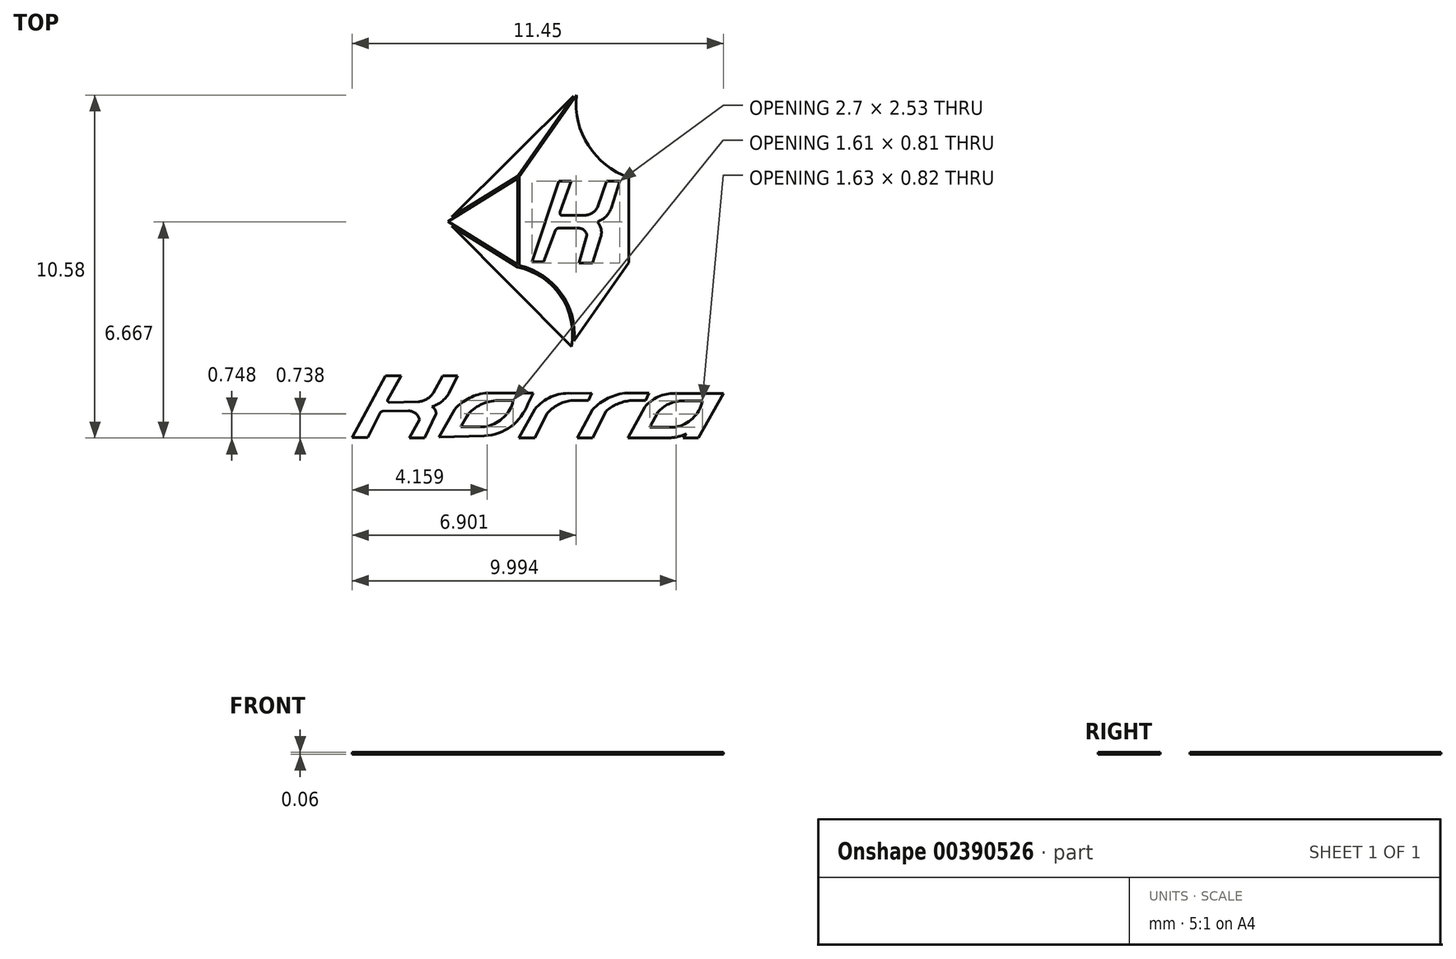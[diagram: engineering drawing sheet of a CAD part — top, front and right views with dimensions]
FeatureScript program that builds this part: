
annotation { "Feature Type Name" : "Feature", "Feature Type Description" : "" }
export const myFeature = defineFeature(function(context is Context, id is Id, definition is map)
    precondition{}
    {
        {
            var Q0;
            Q0=qCreatedBy(makeId("Top.planeOp"),FACE);
            var sketch = newSketch(context, id + "F0", { "sketchPlane" : qUnion([Q0])});
            skLineSegment(sketch, "E0", {"start": v(-5.5, 15.48) * mm, "end": v(-5.5, 6.6) * mm});
            skLineSegment(sketch, "E1", {"start": v(-5.5, 6.36) * mm, "end": v(-12.27, 10.6) * mm});
            skLineSegment(sketch, "E2", {"start": v(-5.5, 15.71) * mm, "end": v(-12.26, 11.53) * mm});
            skLineSegment(sketch, "E3", {"start": v(0.24, 23.94) * mm, "end": v(-5.5, 15.71) * mm});
            skLineSegment(sketch, "E4", {"start": v(0.88, 24.86) * mm, "end": v(-13.01, 11.06) * mm});
            skLineSegment(sketch, "E5", {"start": v(-13.01, 11.06) * mm, "end": v(0, -2.05) * mm});
            skLineSegment(sketch, "E6", {"start": v(0, -2.05) * mm, "end": v(6.14, 6.74) * mm});
            skLineSegment(sketch, "E7", {"start": v(6.14, 6.74) * mm, "end": v(6.14, 15.71) * mm});
            skArc(sketch, "E8", {"start": v(0.88, 24.86) * mm, "mid": v(1.76, 19.28) * mm, "end": v(6.14, 15.71) * mm});
            skArc(sketch, "E9", {"start": v(0.05, -1.81) * mm, "mid": v(-1.08, 3.4) * mm, "end": v(-5.5, 6.36) * mm});
            skLineSegment(sketch, "E10.0", {"start": v(5.94, 6.74) * mm, "end": v(5.94, 15.57) * mm});
            skArc(sketch, "E11.0", {"start": v(0.32, -1.24) * mm, "mid": v(-1.04, 3.7) * mm, "end": v(-5.3, 6.52) * mm});
            skLineSegment(sketch, "E12.0", {"start": v(-5.3, 15.65) * mm, "end": v(-5.3, 6.52) * mm});
            skLineSegment(sketch, "E13.0", {"start": v(0.55, 24.03) * mm, "end": v(-5.3, 15.65) * mm});
            skArc(sketch, "E14.trimOffspring", {"start": v(0.55, 24.03) * mm, "mid": v(1.77, 18.86) * mm, "end": v(5.94, 15.57) * mm});
            skLineSegment(sketch, "E15.trimOffspring", {"start": v(0.32, -1.24) * mm, "end": v(5.97, 6.85) * mm});
            skLineSegment(sketch, "E16.0", {"start": v(0.24, 23.94) * mm, "end": v(-12.26, 11.53) * mm});
            skLineSegment(sketch, "E17.0", {"start": v(-5.5, 15.48) * mm, "end": v(-12.64, 11.06) * mm});
            skLineSegment(sketch, "E18.0", {"start": v(-5.5, 6.6) * mm, "end": v(-12.64, 11.06) * mm});
            skLineSegment(sketch, "E19.trimOffspring", {"start": v(-12.27, 10.6) * mm, "end": v(0.05, -1.81) * mm});
            skLineSegment(sketch, "E20", {"start": v(-1.26, 15.2) * mm, "end": v(-4, 6.89) * mm});
            skLineSegment(sketch, "E21", {"start": v(-4, 6.89) * mm, "end": v(-2.81, 6.89) * mm});
            skLineSegment(sketch, "E22", {"start": v(-1.26, 15.2) * mm, "end": v(0, 15.2) * mm});
            skLineSegment(sketch, "E23", {"start": v(0, 15.2) * mm, "end": v(-1.26, 11.68) * mm});
            skLineSegment(sketch, "E24", {"start": v(-1.26, 11.68) * mm, "end": v(1.4, 11.68) * mm});
            skLineSegment(sketch, "E25", {"start": v(3.63, 15.18) * mm, "end": v(2.75, 12.6) * mm});
            skLineSegment(sketch, "E26", {"start": v(3.63, 15.18) * mm, "end": v(5.01, 15.18) * mm});
            skLineSegment(sketch, "E27", {"start": v(5.01, 15.18) * mm, "end": v(4.14, 12.47) * mm});
            skLineSegment(sketch, "E28", {"start": v(-2.81, 6.89) * mm, "end": v(-1.52, 10.35) * mm});
            skLineSegment(sketch, "E29", {"start": v(-1.52, 10.35) * mm, "end": v(0.78, 10.35) * mm});
            skLineSegment(sketch, "E30", {"start": v(1.64, 9.59) * mm, "end": v(0.82, 6.78) * mm});
            skLineSegment(sketch, "E31", {"start": v(0.82, 6.78) * mm, "end": v(2.2, 6.78) * mm});
            skLineSegment(sketch, "E32", {"start": v(2.2, 6.78) * mm, "end": v(3.05, 9.47) * mm});
            skArc(sketch, "E33", {"start": v(1.4, 11.68) * mm, "mid": v(2.22, 11.93) * mm, "end": v(2.75, 12.6) * mm});
            skArc(sketch, "E34", {"start": v(2.7, 11) * mm, "mid": v(3.6, 11.57) * mm, "end": v(4.14, 12.47) * mm});
            skArc(sketch, "E35", {"start": v(3.05, 9.47) * mm, "mid": v(3.09, 10.28) * mm, "end": v(2.7, 11) * mm});
            skArc(sketch, "E36", {"start": v(1.64, 9.59) * mm, "mid": v(1.36, 10.13) * mm, "end": v(0.78, 10.35) * mm});
            skArc(sketch, "E37", {"start": v(-1.13, 12.04) * mm, "mid": v(-1.13, 11.84) * mm, "end": v(-1.03, 11.68) * mm});
            skArc(sketch, "E38", {"start": v(-1.3, 10.35) * mm, "mid": v(-1.48, 10.29) * mm, "end": v(-1.6, 10.15) * mm});
            skArc(sketch, "E39", {"start": v(-15.71, -7.5) * mm, "mid": v(-14.84, -7.23) * mm, "end": v(-14.17, -6.61) * mm});
            skArc(sketch, "E40", {"start": v(-14.3, -8) * mm, "mid": v(-13.31, -7.49) * mm, "end": v(-12.58, -6.65) * mm});
            skArc(sketch, "E41", {"start": v(-13.9, -8.8) * mm, "mid": v(-13.97, -8.34) * mm, "end": v(-14.3, -8) * mm});
            skArc(sketch, "E42", {"start": v(-18.88, -7.32) * mm, "mid": v(-18.84, -7.48) * mm, "end": v(-18.7, -7.56) * mm});
            skArc(sketch, "E43", {"start": v(-19.32, -8.46) * mm, "mid": v(-19.54, -8.55) * mm, "end": v(-19.69, -8.73) * mm});
            skArc(sketch, "E44", {"start": v(-8.6, -6.6) * mm, "mid": v(-10.45, -7.12) * mm, "end": v(-11.96, -8.29) * mm});
            skArc(sketch, "E45", {"start": v(-8.87, -10.1) * mm, "mid": v(-7.09, -9.25) * mm, "end": v(-5.99, -7.62) * mm});
            skArc(sketch, "E46", {"start": v(0, -7.39) * mm, "mid": v(-1.37, -7.83) * mm, "end": v(-2.49, -8.74) * mm});
            skArc(sketch, "E47", {"start": v(0, -6.63) * mm, "mid": v(-2.05, -7.01) * mm, "end": v(-3.71, -8.27) * mm});
            skArc(sketch, "E48", {"start": v(5.75, -6.6) * mm, "mid": v(3.83, -7.13) * mm, "end": v(2.22, -8.31) * mm});
            skArc(sketch, "E49", {"start": v(6.05, -7.39) * mm, "mid": v(4.75, -7.75) * mm, "end": v(3.62, -8.46) * mm});
            skArc(sketch, "E50", {"start": v(10.64, -6.63) * mm, "mid": v(8.96, -7) * mm, "end": v(7.57, -8.03) * mm});
            skArc(sketch, "E51", {"start": v(11.38, -7.4) * mm, "mid": v(10.04, -7.74) * mm, "end": v(8.95, -8.57) * mm});
            skArc(sketch, "E52", {"start": v(10.45, -10.14) * mm, "mid": v(12.32, -9.38) * mm, "end": v(13.44, -7.7) * mm});
            skArc(sketch, "E53", {"start": v(-8.92, -11) * mm, "mid": v(-6.17, -10.04) * mm, "end": v(-4.44, -7.7) * mm});
            skLineSegment(sketch, "E54", {"start": v(-8.6, -6.6) * mm, "end": v(-3.9, -6.6) * mm});
            skLineSegment(sketch, "E55", {"start": v(-3.9, -6.6) * mm, "end": v(-4.44, -7.7) * mm});
            skLineSegment(sketch, "E56", {"start": v(-8.92, -11) * mm, "end": v(-13.57, -11.15) * mm});
            skLineSegment(sketch, "E57", {"start": v(-13.57, -11.15) * mm, "end": v(-11.96, -8.29) * mm});
            skLineSegment(sketch, "E58", {"start": v(-7.5, -7.39) * mm, "end": v(-5.95, -7.39) * mm});
            skLineSegment(sketch, "E59", {"start": v(-5.95, -7.39) * mm, "end": v(-5.99, -7.62) * mm});
            skLineSegment(sketch, "E60", {"start": v(-8.87, -10.1) * mm, "end": v(-11.33, -10.1) * mm});
            skLineSegment(sketch, "E61", {"start": v(-11.33, -10.1) * mm, "end": v(-10.72, -8.97) * mm});
            skArc(sketch, "E62", {"start": v(-7.5, -7.39) * mm, "mid": v(-9.29, -7.8) * mm, "end": v(-10.72, -8.97) * mm});
            skLineSegment(sketch, "E63", {"start": v(-19.07, -4.84) * mm, "end": v(-22.5, -11.18) * mm});
            skLineSegment(sketch, "E64", {"start": v(-22.5, -11.18) * mm, "end": v(-20.9, -11.18) * mm});
            skLineSegment(sketch, "E65", {"start": v(-20.9, -11.18) * mm, "end": v(-19.69, -8.73) * mm});
            skLineSegment(sketch, "E66", {"start": v(-19.32, -8.46) * mm, "end": v(-16.7, -8.44) * mm});
            skLineSegment(sketch, "E67", {"start": v(-16.62, -11.21) * mm, "end": v(-15.58, -9.33) * mm});
            skArc(sketch, "E68", {"start": v(-15.58, -9.33) * mm, "mid": v(-15.99, -8.69) * mm, "end": v(-16.7, -8.44) * mm});
            skLineSegment(sketch, "E69", {"start": v(-16.62, -11.21) * mm, "end": v(-15.07, -11.21) * mm});
            skLineSegment(sketch, "E70", {"start": v(-15.07, -11.21) * mm, "end": v(-13.9, -8.8) * mm});
            skLineSegment(sketch, "E71", {"start": v(-19.07, -4.84) * mm, "end": v(-17.47, -4.84) * mm});
            skLineSegment(sketch, "E72", {"start": v(-17.47, -4.84) * mm, "end": v(-18.88, -7.32) * mm});
            skLineSegment(sketch, "E73", {"start": v(-18.7, -7.56) * mm, "end": v(-15.71, -7.5) * mm});
            skLineSegment(sketch, "E74", {"start": v(-14.17, -6.61) * mm, "end": v(-13.21, -4.84) * mm});
            skLineSegment(sketch, "E75", {"start": v(-13.21, -4.84) * mm, "end": v(-11.68, -4.84) * mm});
            skLineSegment(sketch, "E76", {"start": v(-11.68, -4.84) * mm, "end": v(-12.58, -6.65) * mm});
            skLineSegment(sketch, "E77", {"start": v(-3.71, -8.27) * mm, "end": v(-5.37, -11.21) * mm});
            skLineSegment(sketch, "E78", {"start": v(-5.37, -11.21) * mm, "end": v(-3.71, -11.24) * mm});
            skLineSegment(sketch, "E79", {"start": v(-3.71, -11.24) * mm, "end": v(-2.49, -8.74) * mm});
            skLineSegment(sketch, "E80", {"start": v(0, -6.63) * mm, "end": v(2.12, -6.61) * mm});
            skLineSegment(sketch, "E81", {"start": v(2.12, -6.61) * mm, "end": v(1.79, -7.39) * mm});
            skLineSegment(sketch, "E82", {"start": v(1.79, -7.39) * mm, "end": v(0, -7.39) * mm});
            skLineSegment(sketch, "E83", {"start": v(2.22, -8.31) * mm, "end": v(0.66, -11.21) * mm});
            skLineSegment(sketch, "E84", {"start": v(0.66, -11.21) * mm, "end": v(2.22, -11.24) * mm});
            skLineSegment(sketch, "E85", {"start": v(2.22, -11.24) * mm, "end": v(3.62, -8.46) * mm});
            skLineSegment(sketch, "E86", {"start": v(5.75, -6.6) * mm, "end": v(8, -6.61) * mm});
            skLineSegment(sketch, "E87", {"start": v(8, -6.61) * mm, "end": v(7.66, -7.39) * mm});
            skLineSegment(sketch, "E88", {"start": v(7.66, -7.39) * mm, "end": v(6.05, -7.39) * mm});
            skLineSegment(sketch, "E89", {"start": v(7.57, -8.03) * mm, "end": v(5.84, -11.24) * mm});
            skLineSegment(sketch, "E90", {"start": v(5.84, -11.24) * mm, "end": v(10.03, -11.21) * mm});
            skLineSegment(sketch, "E91", {"start": v(10.64, -6.63) * mm, "end": v(15.67, -6.64) * mm});
            skLineSegment(sketch, "E92", {"start": v(15.67, -6.64) * mm, "end": v(13.07, -11.21) * mm});
            skLineSegment(sketch, "E93", {"start": v(13.07, -11.21) * mm, "end": v(11.54, -11.21) * mm});
            skLineSegment(sketch, "E94", {"start": v(11.54, -11.21) * mm, "end": v(11.86, -10.78) * mm});
            skArc(sketch, "E95", {"start": v(10.03, -11.21) * mm, "mid": v(10.97, -11.1) * mm, "end": v(11.86, -10.78) * mm});
            skLineSegment(sketch, "E96", {"start": v(11.38, -7.4) * mm, "end": v(13.52, -7.4) * mm});
            skLineSegment(sketch, "E97", {"start": v(13.52, -7.4) * mm, "end": v(13.44, -7.7) * mm});
            skLineSegment(sketch, "E98", {"start": v(10.45, -10.14) * mm, "end": v(8.1, -10.14) * mm});
            skLineSegment(sketch, "E99", {"start": v(8.1, -10.14) * mm, "end": v(8.95, -8.57) * mm});
            skSolve(sketch);
        }
        {
            var Q0;
            {var subQ8=sQuery(id+"F0.wireOp",EDGE,"E11.0");Q0=makeQuery(id+"F0.imprint","IMPRINT",FACE,{"disambiguationData":[TD([[makeQuery(id+"F0.imprint","IMPRINT",EDGE,{"derivedFrom":subQ8}),-1.0]])]});}
            var Q1;
            Q1=makeQuery(id+"F0.imprint","IMPRINT",FACE,{"disambiguationData":[TD([[makeQuery(id+"F0.imprint","IMPRINT",EDGE,{"derivedFrom":sQuery(id+"F0.wireOp",EDGE,"E1")}),1.0]])]});
            var Q2;
            Q2=makeQuery(id+"F0.imprint","IMPRINT",FACE,{"disambiguationData":[TD([[makeQuery(id+"F0.imprint","IMPRINT",EDGE,{"derivedFrom":sQuery(id+"F0.wireOp",EDGE,"E0")}),-1.0]])]});
            var Q3;
            Q3=makeQuery(id+"F0.imprint","IMPRINT",FACE,{"disambiguationData":[TD([[makeQuery(id+"F0.imprint","IMPRINT",EDGE,{"derivedFrom":sQuery(id+"F0.wireOp",EDGE,"E2")}),-1.0]])]});
            var Q4;
            Q4=makeQuery(id+"F0.imprint","IMPRINT",FACE,{"disambiguationData":[TD([[makeQuery(id+"F0.imprint","IMPRINT",EDGE,{"derivedFrom":sQuery(id+"F0.wireOp",EDGE,"E50")}),1.0]])]});
            var Q5;
            Q5=makeQuery(id+"F0.imprint","IMPRINT",FACE,{"disambiguationData":[TD([[makeQuery(id+"F0.imprint","IMPRINT",EDGE,{"derivedFrom":sQuery(id+"F0.wireOp",EDGE,"E48")}),1.0]])]});
            var Q6;
            Q6=makeQuery(id+"F0.imprint","IMPRINT",FACE,{"disambiguationData":[TD([[makeQuery(id+"F0.imprint","IMPRINT",EDGE,{"derivedFrom":sQuery(id+"F0.wireOp",EDGE,"E46")}),-1.0]])]});
            var Q7;
            Q7=makeQuery(id+"F0.imprint","IMPRINT",FACE,{"disambiguationData":[TD([[makeQuery(id+"F0.imprint","IMPRINT",EDGE,{"derivedFrom":sQuery(id+"F0.wireOp",EDGE,"E44")}),1.0]])]});
            var Q8;
            Q8=makeQuery(id+"F0.imprint","IMPRINT",FACE,{"disambiguationData":[TD([[makeQuery(id+"F0.imprint","IMPRINT",EDGE,{"derivedFrom":sQuery(id+"F0.wireOp",EDGE,"E39")}),-1.0]])]});
            extrude(context, id + "F1", {"entities" : qUnion([Q0, Q1, Q2, Q3, Q4, Q5, Q6, Q7, Q8]), "oppositeDirection" : true, "depth" : .2 * mm});
        }
        {
            var Q0;
            Q0=makeQuery(id+"F1.opExtrude","SWEPT_BODY",BODY,{"disambiguationData":[OSD([sQuery(id+"F0.wireOp",EDGE,"E1"),sQuery(id+"F0.wireOp",EDGE,"E9"),sQuery(id+"F0.wireOp",EDGE,"E19.trimOffspring")])]});
            var Q1;
            Q1=makeQuery(id+"F1.opExtrude","SWEPT_BODY",BODY,{"disambiguationData":[OSD([sQuery(id+"F0.wireOp",EDGE,"E39"),sQuery(id+"F0.wireOp",EDGE,"E40"),sQuery(id+"F0.wireOp",EDGE,"E41"),sQuery(id+"F0.wireOp",EDGE,"E42"),sQuery(id+"F0.wireOp",EDGE,"E43"),sQuery(id+"F0.wireOp",EDGE,"E63"),sQuery(id+"F0.wireOp",EDGE,"E64"),sQuery(id+"F0.wireOp",EDGE,"E65"),sQuery(id+"F0.wireOp",EDGE,"E66"),sQuery(id+"F0.wireOp",EDGE,"E67"),sQuery(id+"F0.wireOp",EDGE,"E68"),sQuery(id+"F0.wireOp",EDGE,"E69"),sQuery(id+"F0.wireOp",EDGE,"E70"),sQuery(id+"F0.wireOp",EDGE,"E71"),sQuery(id+"F0.wireOp",EDGE,"E72"),sQuery(id+"F0.wireOp",EDGE,"E73"),sQuery(id+"F0.wireOp",EDGE,"E74"),sQuery(id+"F0.wireOp",EDGE,"E75"),sQuery(id+"F0.wireOp",EDGE,"E76")])]});
            var Q2;
            Q2=makeQuery(id+"F1.opExtrude","SWEPT_BODY",BODY,{"disambiguationData":[OSD([sQuery(id+"F0.wireOp",EDGE,"E44"),sQuery(id+"F0.wireOp",EDGE,"E45"),sQuery(id+"F0.wireOp",EDGE,"E53"),sQuery(id+"F0.wireOp",EDGE,"E54"),sQuery(id+"F0.wireOp",EDGE,"E55"),sQuery(id+"F0.wireOp",EDGE,"E56"),sQuery(id+"F0.wireOp",EDGE,"E57"),sQuery(id+"F0.wireOp",EDGE,"E58"),sQuery(id+"F0.wireOp",EDGE,"E59"),sQuery(id+"F0.wireOp",EDGE,"E60"),sQuery(id+"F0.wireOp",EDGE,"E61"),sQuery(id+"F0.wireOp",EDGE,"E62")])]});
            var Q3;
            Q3=makeQuery(id+"F1.opExtrude","SWEPT_BODY",BODY,{"disambiguationData":[OSD([sQuery(id+"F0.wireOp",EDGE,"E46"),sQuery(id+"F0.wireOp",EDGE,"E47"),sQuery(id+"F0.wireOp",EDGE,"E77"),sQuery(id+"F0.wireOp",EDGE,"E78"),sQuery(id+"F0.wireOp",EDGE,"E79"),sQuery(id+"F0.wireOp",EDGE,"E80"),sQuery(id+"F0.wireOp",EDGE,"E81"),sQuery(id+"F0.wireOp",EDGE,"E82")])]});
            var Q4;
            Q4=makeQuery(id+"F1.opExtrude","SWEPT_BODY",BODY,{"disambiguationData":[OSD([sQuery(id+"F0.wireOp",EDGE,"E0"),sQuery(id+"F0.wireOp",EDGE,"E17.0"),sQuery(id+"F0.wireOp",EDGE,"E18.0")])]});
            var Q5;
            Q5=makeQuery(id+"F1.opExtrude","SWEPT_BODY",BODY,{"disambiguationData":[OSD([sQuery(id+"F0.wireOp",EDGE,"E2"),sQuery(id+"F0.wireOp",EDGE,"E3"),sQuery(id+"F0.wireOp",EDGE,"E16.0")])]});
            var Q6;
            Q6=makeQuery(id+"F1.opExtrude","SWEPT_BODY",BODY,{"disambiguationData":[OSD([sQuery(id+"F0.wireOp",EDGE,"E10.0"),sQuery(id+"F0.wireOp",EDGE,"E11.0"),sQuery(id+"F0.wireOp",EDGE,"E12.0"),sQuery(id+"F0.wireOp",EDGE,"E13.0"),sQuery(id+"F0.wireOp",EDGE,"E14.trimOffspring"),sQuery(id+"F0.wireOp",EDGE,"E15.trimOffspring"),sQuery(id+"F0.wireOp",EDGE,"E20"),sQuery(id+"F0.wireOp",EDGE,"E21"),sQuery(id+"F0.wireOp",EDGE,"E22"),sQuery(id+"F0.wireOp",EDGE,"E23"),sQuery(id+"F0.wireOp",EDGE,"E24"),sQuery(id+"F0.wireOp",EDGE,"E25"),sQuery(id+"F0.wireOp",EDGE,"E26"),sQuery(id+"F0.wireOp",EDGE,"E27"),sQuery(id+"F0.wireOp",EDGE,"E28"),sQuery(id+"F0.wireOp",EDGE,"E29"),sQuery(id+"F0.wireOp",EDGE,"E30"),sQuery(id+"F0.wireOp",EDGE,"E31"),sQuery(id+"F0.wireOp",EDGE,"E32"),sQuery(id+"F0.wireOp",EDGE,"E33"),sQuery(id+"F0.wireOp",EDGE,"E34"),sQuery(id+"F0.wireOp",EDGE,"E35"),sQuery(id+"F0.wireOp",EDGE,"E36"),sQuery(id+"F0.wireOp",EDGE,"E37"),sQuery(id+"F0.wireOp",EDGE,"E38")])]});
            var Q7;
            Q7=makeQuery(id+"F1.opExtrude","SWEPT_BODY",BODY,{"disambiguationData":[OSD([sQuery(id+"F0.wireOp",EDGE,"E48"),sQuery(id+"F0.wireOp",EDGE,"E49"),sQuery(id+"F0.wireOp",EDGE,"E83"),sQuery(id+"F0.wireOp",EDGE,"E84"),sQuery(id+"F0.wireOp",EDGE,"E85"),sQuery(id+"F0.wireOp",EDGE,"E86"),sQuery(id+"F0.wireOp",EDGE,"E87"),sQuery(id+"F0.wireOp",EDGE,"E88")])]});
            var Q8;
            Q8=makeQuery(id+"F1.opExtrude","SWEPT_BODY",BODY,{"disambiguationData":[OSD([sQuery(id+"F0.wireOp",EDGE,"E50"),sQuery(id+"F0.wireOp",EDGE,"E51"),sQuery(id+"F0.wireOp",EDGE,"E52"),sQuery(id+"F0.wireOp",EDGE,"E89"),sQuery(id+"F0.wireOp",EDGE,"E90"),sQuery(id+"F0.wireOp",EDGE,"E91"),sQuery(id+"F0.wireOp",EDGE,"E92"),sQuery(id+"F0.wireOp",EDGE,"E93"),sQuery(id+"F0.wireOp",EDGE,"E94"),sQuery(id+"F0.wireOp",EDGE,"E95"),sQuery(id+"F0.wireOp",EDGE,"E96"),sQuery(id+"F0.wireOp",EDGE,"E97"),sQuery(id+"F0.wireOp",EDGE,"E98"),sQuery(id+"F0.wireOp",EDGE,"E99")])]});
            var Q9;
            Q9=qCreatedBy(makeId("Origin.pointOp"),VERTEX);
            transform(context, id + "F2", {"entities" : qUnion([Q0, Q1, Q2, Q3, Q4, Q5, Q6, Q7, Q8]), "transformType" : TransformType.SCALE_UNIFORMLY, "scale" : .3, "scalePoint" : qUnion([Q9]), "makeCopy" : false});
        }
    });
